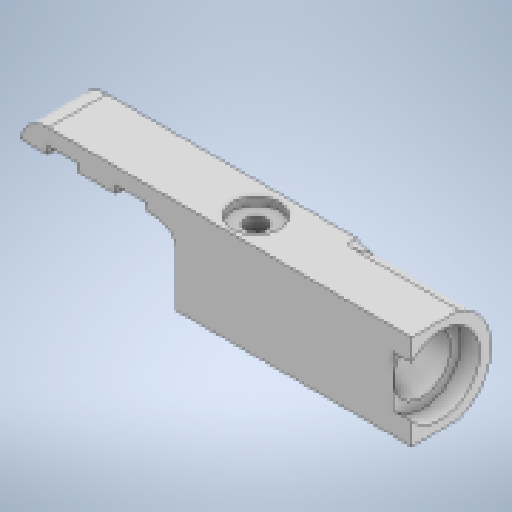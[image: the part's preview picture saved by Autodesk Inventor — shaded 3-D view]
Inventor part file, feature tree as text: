
AUTODESK INVENTOR PART (.ipt)
format: ipt  version: 2023.3 (Build 273359000, 359)  size: 307,712 bytes
history: native  units: in
note: dims shown in document units (in); Inventor stores cm internally (conversion verified against a paired STEP export)
features: extrude x10, sketch x9, reference x7, other x3, fillet x1, projected_geometry x1
ambient origin geometry x8: Origin, YZ Plane, XZ Plane, XY Plane, X Axis, Y Axis, Z Axis, Center Point
bodies: Solid1 (feature_tree)
feature tree (31):
  extrude  "Extrusion1"  Depth=0.0984in
  extrude  "Extrusion2"  Depth=0.0787in
  extrude  "Extrusion3"  Depth=1.1614in
  extrude  "Extrusion4"  Depth=0.0472in TaperAngle=0.0deg
  extrude  "Extrusion5"  Depth=0.0079in
  extrude  "Extrusion6"  Depth=0.0394in
  extrude  "Extrusion7"  Depth=0.0394in
  extrude  "screw_hole"  Depth=0.3937in
  fillet  "Fillet1"  Radius=0.3937in
  extrude  "Extrusion9"  Depth=0.1969in
  extrude  "Extrusion10"  Depth=0.4134in TaperAngle=0.0deg
  sketch  "Sketch1"  dims[d1=0.0354in d2=0.0984in]
  reference  "Reference1"
  reference  "Reference2"
  reference  "Reference3"
  sketch  "Sketch2"  dims[d3=0.5118in d4=0.0787in]
  reference  "Reference4"
  reference  "Reference5"
  sketch  "Sketch3"  dims[d5=0.1181in d6=1.1614in]
  sketch  "Sketch5"  dims[d7=0.374in d8=0.0472in d9=0.1969in d10=0.0in d11=0.0in]
  sketch  "Sketch6"  dims[d12=0.0236in d13=0.0079in d14=0.0079in]
  sketch  "Sketch7"  dims[d15=0.0315in d16=0.0in d17=0.0394in]
  sketch  "Sketch8"  dims[d18=0.1181in d19=0.0394in]
  sketch  "Sketch9"  dims[d20=0.315in d21=0.0in d22=0.122in d23=0.3937in]
  projected_geometry  "Projected Loop1"
  reference  "Reference6"
  sketch  "Sketch10"  dims[d24=0.2441in d25=0.1969in d26=0.4134in d27=0.4724in d28=0.0in d29=0.3228in d30=0.0787in d31=0.0in d32=0.2402in d33=0.315in d34=0.0in d35=0.1181in d36=0.315in d37=0.0in d38=0.1969in d39=0.7874in d40=0.1378in d41=0.0in d42=0.0in d43=0.0787in d44=0.0866in d45=0.4724in d46=0.0in d47=0.0079in d48=0.0079in d49=0.1969in d50=0.0315in d51=0.0in d52=0.0079in]
  reference  "Reference7"
  parser-record x1  (decoder bookkeeping rows leaked as tree rows — omitted from the tree; the rows remain in map.json)
  other  "np2a_assembly.iam"
  other  "np2a:1"
note: 1 file-system path scrubbed to <path> (originals preserved in map.json)
